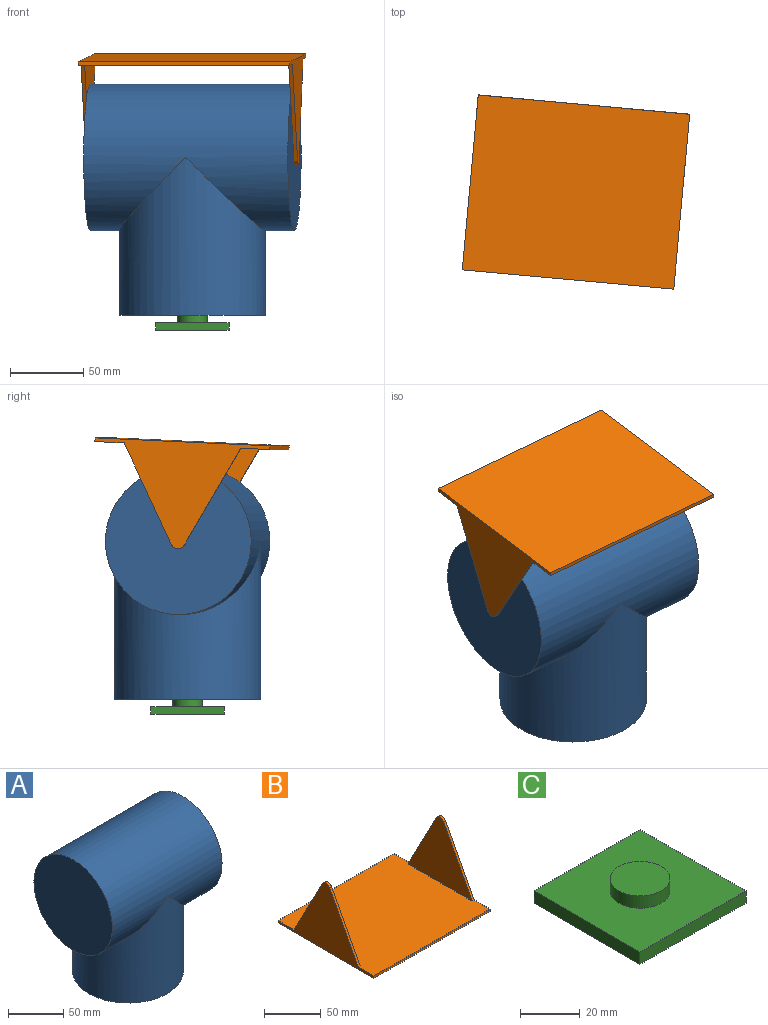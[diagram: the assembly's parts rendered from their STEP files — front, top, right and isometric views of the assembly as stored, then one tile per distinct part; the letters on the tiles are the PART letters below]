
ASSEMBLY  parts=3 mates=2
PART A: 5 faces, bbox 140x100x158 mm
  f0: cylinder r=50mm len=108mm, axis (0,0,-1), area 23929.2mm2, adj f1,f2
  f1: plane 100x100mm, normal (0,0,-1), area 7854mm2, adj f0
  f2: cylinder r=50mm len=140mm, axis (-1,0,0), area 33982.3mm2, adj f0,f3,f4
  f3: plane 100x100mm, normal (1,0,0), area 7854mm2, adj f2
  f4: plane 100x100mm, normal (-1,0,0), area 7854mm2, adj f2
PART B: 14 faces, bbox 145x120x73 mm
  f0: plane 145x2.5mm, normal (0,-1,0), area 362.5mm2, adj f1,f3,f4,f5
  f1: plane 120x73mm, normal (1,0,0), area 3330.1mm2, adj f0,f2,f4,f5,f6,f7,f8
  f2: plane 145x2.5mm, normal (0,1,0), area 362.5mm2, adj f1,f3,f4,f5
  f3: plane 120x73mm, normal (-1,0,0), area 3330.1mm2, adj f0,f2,f4,f5,f10,f11,f12
  f4: plane 145x120mm, normal (0,0,1), area 17000mm2, adj f0,f1,f2,f3,f6,f7,f9,f10
  f5: plane 145x120mm, normal (0,0,-1), area 17400mm2, adj f0,f1,f2,f3
  f6: plane 67.82x35.57mm, normal (0,-0.89,0.46), area 191.5mm2, adj f1,f4,f8,f9
  f7: plane 67.82x35.57mm, normal (0,0.89,0.46), area 191.5mm2, adj f1,f4,f8,f9
  f8: cylinder r=5mm len=8.86mm, axis (1,0,0), area 27.2mm2, adj f1,f6,f7,f9
  f9: plane 80x70.5mm, normal (-1,0,0), area 3030.1mm2, adj f4,f6,f7,f8
  f10: plane 67.82x35.57mm, normal (0,-0.89,0.46), area 191.5mm2, adj f3,f4,f11,f13
  f11: cylinder r=5mm len=8.86mm, axis (-1,0,0), area 27.2mm2, adj f3,f10,f12,f13
  f12: plane 67.82x35.57mm, normal (0,0.89,0.46), area 191.5mm2, adj f3,f4,f11,f13
  f13: plane 80x70.5mm, normal (1,0,0), area 3030.1mm2, adj f4,f10,f11,f12
PART C: 8 faces, bbox 50x50x10 mm
  f0: plane 50x5mm, normal (0,-1,0), area 250mm2, adj f1,f3,f4,f5
  f1: plane 50x5mm, normal (1,0,0), area 250mm2, adj f0,f2,f4,f5
  f2: plane 50x5mm, normal (0,1,0), area 250mm2, adj f1,f3,f4,f5
  f3: plane 50x5mm, normal (-1,0,0), area 250mm2, adj f0,f2,f4,f5
  f4: plane 50x50mm, normal (0,0,1), area 2185.8mm2, adj f0,f1,f2,f3,f6
  f5: plane 50x50mm, normal (0,0,-1), area 2500mm2, adj f0,f1,f2,f3
  f6: cylinder r=10mm len=20mm, axis (0,0,-1), area 314.2mm2, adj f4,f7
  f7: plane 20x20mm, normal (0,0,1), area 314.2mm2, adj f6
PLACE A rot(axis=(0,0,1),174.8deg) t=(0.18,0,4.84)mm
PLACE B rot(axis=(0.05,1,0.02),179.9deg) t=(-0.1,-3.07,180.77)mm
PLACE C t=(0.18,0,-5.16)mm fixed
MATE revolute A.f2 <-> B.f8  axis (1,-0.09,0) through (69.9,-6.34,112.84)mm
MATE revolute A.f0 <-> C.f6  axis (0,0,-1) through (0.18,0,4.84)mm
